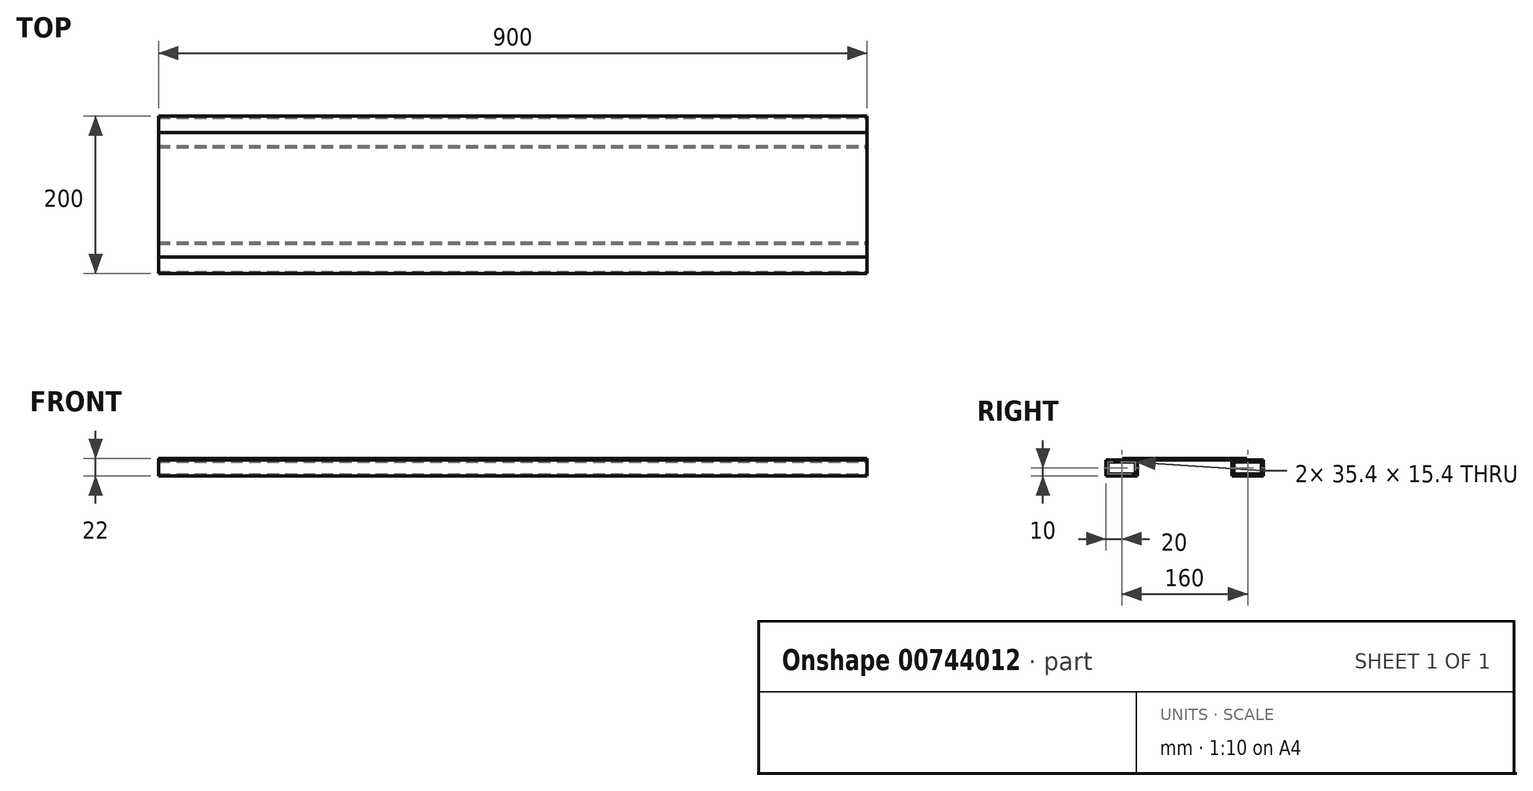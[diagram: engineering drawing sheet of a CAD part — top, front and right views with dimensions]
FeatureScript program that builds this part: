
annotation { "Feature Type Name" : "Feature", "Feature Type Description" : "" }
export const myFeature = defineFeature(function(context is Context, id is Id, definition is map)
    precondition{}
    {
        {
            var Q0;
            Q0=qCreatedBy(makeId("Right.planeOp"),FACE);
            var sketch = newSketch(context, id + "F0", { "sketchPlane" : qUnion([Q0])});
            skLineSegment(sketch, "E0.bottom", {"start": v(20, 10) * mm, "end": v(-20, 10) * mm});
            skLineSegment(sketch, "E0.top", {"start": v(20, -10) * mm, "end": v(-20, -10) * mm});
            skLineSegment(sketch, "E0.left", {"start": v(20, 10) * mm, "end": v(20, -10) * mm});
            skLineSegment(sketch, "E0.right", {"start": v(-20, 10) * mm, "end": v(-20, -10) * mm});
            skPoint(sketch, "E0.middle", {"position": v(0, 0) * mm});
            skLineSegment(sketch, "E1.0", {"start": v(-17.7, 7.7) * mm, "end": v(-17.7, -7.7) * mm});
            skLineSegment(sketch, "E1.1", {"start": v(17.7, 7.7) * mm, "end": v(-17.7, 7.7) * mm});
            skLineSegment(sketch, "E1.2", {"start": v(17.7, 7.7) * mm, "end": v(17.7, -7.7) * mm});
            skLineSegment(sketch, "E1.3", {"start": v(17.7, -7.7) * mm, "end": v(-17.7, -7.7) * mm});
            skLineSegment(sketch, "E2.1.0.0", {"start": v(177.7, 7.7) * mm, "end": v(177.7, -7.7) * mm});
            skLineSegment(sketch, "E2.1.0.1", {"start": v(177.7, -7.7) * mm, "end": v(142.3, -7.7) * mm});
            skLineSegment(sketch, "E2.1.0.2", {"start": v(177.7, 7.7) * mm, "end": v(142.3, 7.7) * mm});
            skPoint(sketch, "E2.1.0.3", {"position": v(160, 0) * mm});
            skLineSegment(sketch, "E2.1.0.4", {"start": v(180, 10) * mm, "end": v(140, 10) * mm});
            skLineSegment(sketch, "E2.1.0.5", {"start": v(180, -10) * mm, "end": v(140, -10) * mm});
            skLineSegment(sketch, "E2.1.0.6", {"start": v(180, 10) * mm, "end": v(180, -10) * mm});
            skLineSegment(sketch, "E2.1.0.7", {"start": v(140, 10) * mm, "end": v(140, -10) * mm});
            skLineSegment(sketch, "E2.1.0.8", {"start": v(142.3, 7.7) * mm, "end": v(142.3, -7.7) * mm});
            skLineSegment(sketch, "E2.direction1", {"start": v(-20, -10) * mm, "end": v(140, -10) * mm, "construction": true});
            skSolve(sketch);
        }
        {
            var Q0;
            Q0=qSketchRegion(id+"F0",true);
            extrude(context, id + "F1", {"entities" : qUnion([Q0]), "oppositeDirection" : true, "depth" : 900 * mm, "offsetDistance" : 25 * mm});
        }
        {
            var Q0;
            Q0=qCreatedBy(makeId("Right.planeOp"),FACE);
            var sketch = newSketch(context, id + "F2", { "sketchPlane" : qUnion([Q0])});
            skLineSegment(sketch, "E3.bottom", {"start": v(1, 12) * mm, "end": v(159, 12) * mm});
            skLineSegment(sketch, "E3.top", {"start": v(1, 10) * mm, "end": v(159, 10) * mm});
            skLineSegment(sketch, "E3.left", {"start": v(1, 12) * mm, "end": v(1, 10) * mm});
            skLineSegment(sketch, "E3.right", {"start": v(159, 12) * mm, "end": v(159, 10) * mm});
            skSolve(sketch);
        }
        {
            var Q0;
            Q0 = qSketchRegion(id + "F2", true);
            extrude(context, id + "F3", {"entities" : qUnion([Q0]), "oppositeDirection" : true, "depth" : 900 * mm, "offsetDistance" : 25 * mm});
        }
    });
